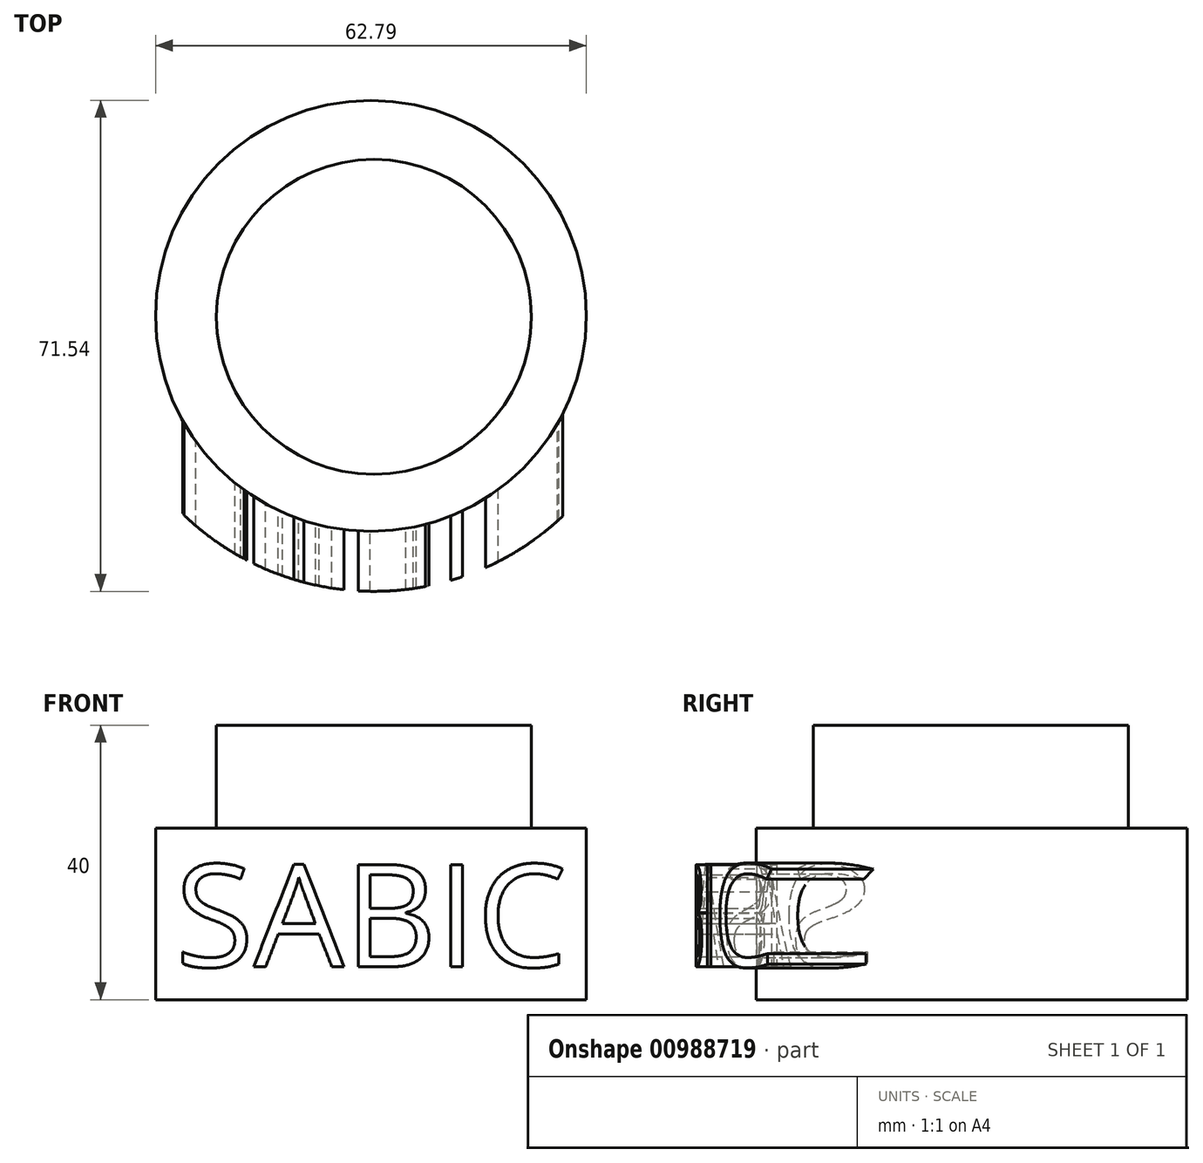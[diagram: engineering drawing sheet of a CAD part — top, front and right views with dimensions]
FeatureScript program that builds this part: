
annotation { "Feature Type Name" : "Feature", "Feature Type Description" : "" }
export const myFeature = defineFeature(function(context is Context, id is Id, definition is map)
    precondition{}
    {
        {
            var Q0;
            Q0=qCreatedBy(makeId("Top.planeOp"),FACE);
            var sketch = newSketch(context, id + "F0", { "sketchPlane" : qUnion([Q0])});
            skCircle(sketch, "E0", {"center": v(-0.42, 0.14) * mm, "radius": 31.4 * mm});
            skSolve(sketch);
        }
        {
            var Q0;
            Q0 = qSketchRegion(id + "F0", true);
            extrude(context, id + "F1", {"entities" : qUnion([Q0]), "depth" : 25 * mm, "offsetDistance" : 25 * mm});
        }
        {
            var Q0;
            Q0=makeQuery(id+"F1.opExtrude","CAP_FACE",FACE,{"disambiguationData":[OSD([sQuery(id+"F0.wireOp",EDGE,"E0")])],"isStart":false});
            var sketch = newSketch(context, id + "F2", { "sketchPlane" : qUnion([Q0])});
            skCircle(sketch, "E1", {"center": v(0, 0) * mm, "radius": 22.94 * mm});
            skSolve(sketch);
        }
        {
            var Q0;
            Q0 = qSketchRegion(id + "F2", true);
            extrude(context, id + "F3", {"entities" : qUnion([Q0]), "operationType" : NewBodyOperationType.ADD, "depth" : 15 * mm, "offsetDistance" : 25 * mm});
        }
        {
            var Q0;
            Q0=makeQuery(id+"F3.opExtrude","CAP_FACE",FACE,{"disambiguationData":[OSD([sQuery(id+"F2.wireOp",EDGE,"E1")])],"isStart":false});
            var sketch = newSketch(context, id + "F4", { "sketchPlane" : qUnion([Q0])});
            skCircle(sketch, "E2", {"center": v(0, 0) * mm, "radius": 13.8 * mm});
            skSolve(sketch);
        }
        {
            var Q0;
            Q0=sQuery(id+"F4.wireOp",EDGE,"E2");
            extrude(context, id + "F5", {"bodyType" : ToolBodyType.SURFACE, "surfaceEntities" : qUnion([Q0]), "depth" : 10 * mm, "offsetDistance" : 25 * mm});
        }
        {
            var Q0;
            Q0=qCreatedBy(makeId("Front.planeOp"),FACE);
            var sketch = newSketch(context, id + "F6", { "sketchPlane" : qUnion([Q0])});
            skText(sketch, "E3", { "text": "SABIC ", "fontName": "OpenSans-Regular.ttf"});
            const initialGuessF6  = {"E3": [-0.02895, 0.00481, 1, 0, 0.015]};
            skSetInitialGuess(sketch, initialGuessF6);
            skSolve(sketch);
        }
        {
            var Q0;
            Q0 = qSketchRegion(id + "F6", true);
            extrude(context, id + "F7", {"entities" : qUnion([Q0]), "operationType" : NewBodyOperationType.ADD, "depth" : 50 * mm, "offsetDistance" : 25 * mm});
        }
        {
            var Q0;
            Q0=qCreatedBy(makeId("Top.planeOp"),FACE);
            var sketch = newSketch(context, id + "F8", { "sketchPlane" : qUnion([Q0])});
            skCircle(sketch, "E4", {"center": v(0, 0) * mm, "radius": 40 * mm});
            skSolve(sketch);
        }
        {
            var Q0;
            Q0 = qSketchRegion(id + "F8", true);
            extrude(context, id + "F9", {"entities" : qUnion([Q0]), "operationType" : NewBodyOperationType.INTERSECT, "depth" : 65 * mm, "offsetDistance" : 25 * mm});
        }
    });
